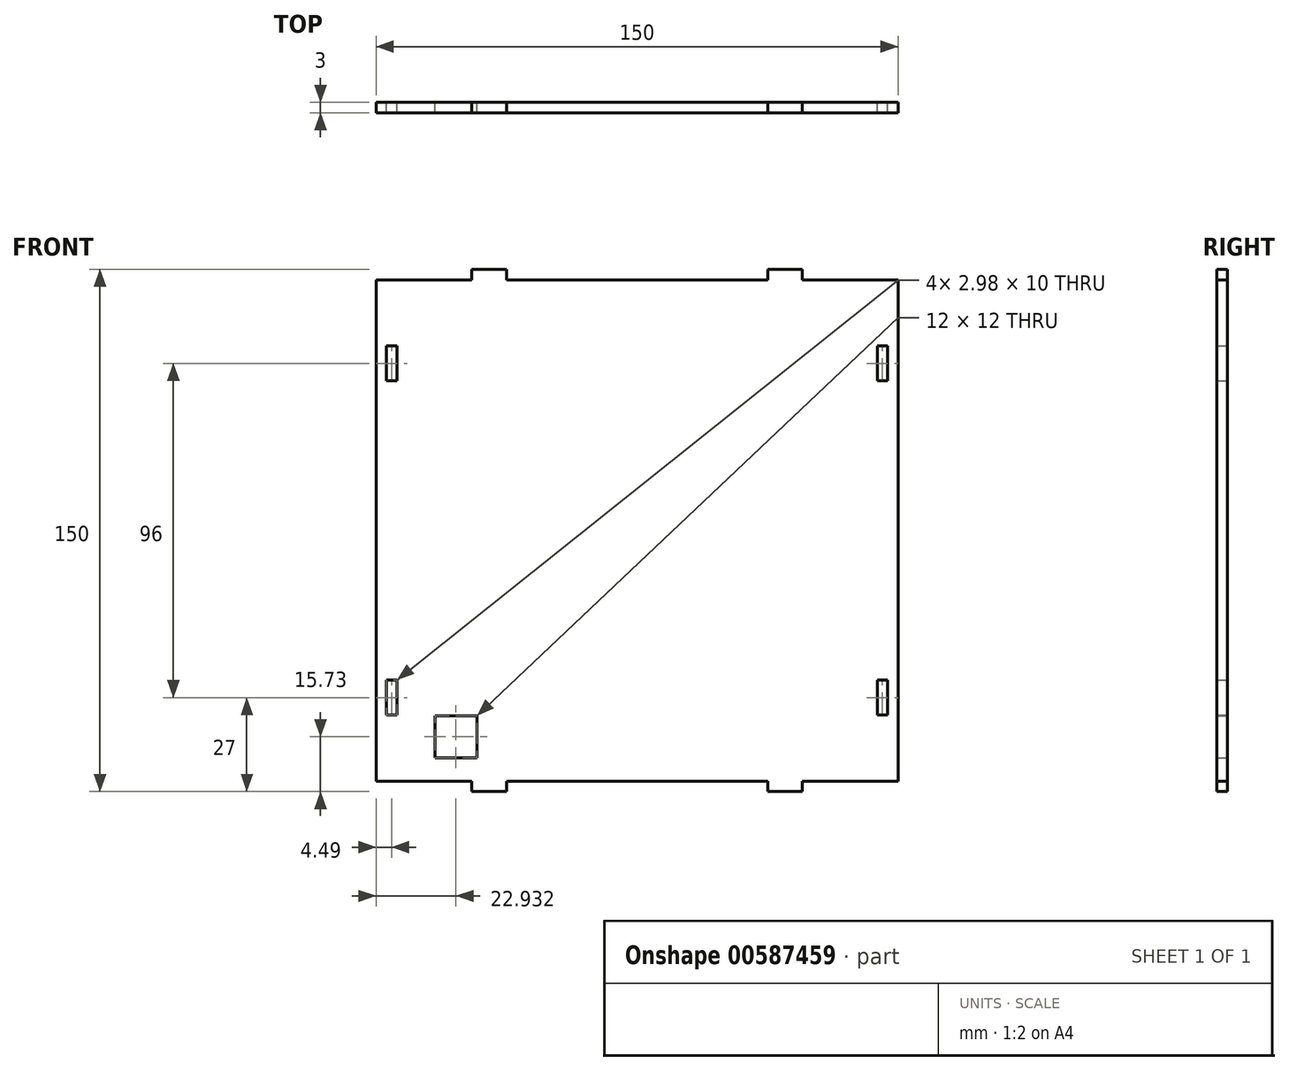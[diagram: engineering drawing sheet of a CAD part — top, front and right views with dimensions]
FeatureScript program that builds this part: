
annotation { "Feature Type Name" : "Feature", "Feature Type Description" : "" }
export const myFeature = defineFeature(function(context is Context, id is Id, definition is map)
    precondition{}
    {
        {
            var Q0;
            Q0=qCreatedBy(makeId("Front.planeOp"),FACE);
            var sketch = newSketch(context, id + "F0", { "sketchPlane" : qUnion([Q0])});
            skLineSegment(sketch, "E0.left", {"start": v(-75, 72) * mm, "end": v(-75, -72) * mm});
            skLineSegment(sketch, "E0.right", {"start": v(75, 72) * mm, "end": v(75, -72) * mm});
            skLineSegment(sketch, "E1", {"start": v(-75, -72) * mm, "end": v(-47.5, -72) * mm});
            skLineSegment(sketch, "E2", {"start": v(-47.5, -72) * mm, "end": v(-47.5, -75) * mm});
            skLineSegment(sketch, "E3", {"start": v(-47.5, -75) * mm, "end": v(-37.5, -75) * mm});
            skLineSegment(sketch, "E4", {"start": v(-37.5, -75) * mm, "end": v(-37.5, -72) * mm});
            skLineSegment(sketch, "E5", {"start": v(-37.5, -72) * mm, "end": v(37.5, -72) * mm});
            skLineSegment(sketch, "E6", {"start": v(37.5, -72) * mm, "end": v(37.5, -75) * mm});
            skLineSegment(sketch, "E7", {"start": v(37.5, -75) * mm, "end": v(47.5, -75) * mm});
            skLineSegment(sketch, "E8", {"start": v(47.5, -75) * mm, "end": v(47.5, -72) * mm});
            skLineSegment(sketch, "E9", {"start": v(47.5, -72) * mm, "end": v(75, -72) * mm});
            skLineSegment(sketch, "E10", {"start": v(0, 72) * mm, "end": v(0, -70.83) * mm, "construction": true});
            skLineSegment(sketch, "E11.bottom", {"start": v(-72, 53) * mm, "end": v(-69.02, 53) * mm});
            skLineSegment(sketch, "E11.top", {"start": v(-72, 43) * mm, "end": v(-69.02, 43) * mm});
            skLineSegment(sketch, "E11.left", {"start": v(-72, 53) * mm, "end": v(-72, 43) * mm});
            skLineSegment(sketch, "E11.right", {"start": v(-69.02, 53) * mm, "end": v(-69.02, 43) * mm});
            skLineSegment(sketch, "E12", {"start": v(-70.51, 53) * mm, "end": v(-70.51, 43) * mm, "construction": true});
            skLineSegment(sketch, "E13", {"start": v(-72, 48) * mm, "end": v(-69.02, 48) * mm, "construction": true});
            skLineSegment(sketch, "E14", {"start": v(75, 0) * mm, "end": v(-75, 0) * mm, "construction": true});
            skLineSegment(sketch, "E15.MirrorCS", {"start": v(72, 43) * mm, "end": v(69.02, 43) * mm});
            skLineSegment(sketch, "E16.MirrorCS", {"start": v(69.02, 53) * mm, "end": v(69.02, 43) * mm});
            skLineSegment(sketch, "E17.MirrorCS", {"start": v(72, 53) * mm, "end": v(69.02, 53) * mm});
            skLineSegment(sketch, "E18.MirrorCS", {"start": v(72, 48) * mm, "end": v(69.02, 48) * mm, "construction": true});
            skLineSegment(sketch, "E19.MirrorCS", {"start": v(72, 53) * mm, "end": v(72, 43) * mm});
            skLineSegment(sketch, "E20.MirrorCS", {"start": v(70.51, 53) * mm, "end": v(70.51, 43) * mm, "construction": true});
            skLineSegment(sketch, "E21.MirrorCS", {"start": v(72, -43) * mm, "end": v(69.02, -43) * mm});
            skLineSegment(sketch, "E22.MirrorCS", {"start": v(72, -53) * mm, "end": v(69.02, -53) * mm});
            skLineSegment(sketch, "E23.MirrorCS", {"start": v(69.02, -53) * mm, "end": v(69.02, -43) * mm});
            skLineSegment(sketch, "E24.MirrorCS", {"start": v(70.51, -53) * mm, "end": v(70.51, -43) * mm, "construction": true});
            skLineSegment(sketch, "E25.MirrorCS", {"start": v(72, -48) * mm, "end": v(69.02, -48) * mm, "construction": true});
            skLineSegment(sketch, "E26.MirrorCS", {"start": v(72, -53) * mm, "end": v(72, -43) * mm});
            skLineSegment(sketch, "E27.MirrorCS", {"start": v(-72, -43) * mm, "end": v(-69.02, -43) * mm});
            skLineSegment(sketch, "E28.MirrorCS", {"start": v(-72, -53) * mm, "end": v(-69.02, -53) * mm});
            skLineSegment(sketch, "E29.MirrorCS", {"start": v(-69.02, -53) * mm, "end": v(-69.02, -43) * mm});
            skLineSegment(sketch, "E30.MirrorCS", {"start": v(-70.51, -53) * mm, "end": v(-70.51, -43) * mm, "construction": true});
            skLineSegment(sketch, "E31.MirrorCS", {"start": v(-72, -48) * mm, "end": v(-69.02, -48) * mm, "construction": true});
            skLineSegment(sketch, "E32.MirrorCS", {"start": v(-72, -53) * mm, "end": v(-72, -43) * mm});
            skLineSegment(sketch, "E33", {"start": v(-75, 72) * mm, "end": v(-47.5, 72) * mm});
            skLineSegment(sketch, "E34", {"start": v(-47.5, 72) * mm, "end": v(-47.5, 75) * mm});
            skLineSegment(sketch, "E35", {"start": v(-47.5, 75) * mm, "end": v(-37.5, 75) * mm});
            skLineSegment(sketch, "E36", {"start": v(-37.5, 75) * mm, "end": v(-37.5, 72) * mm});
            skLineSegment(sketch, "E37", {"start": v(-37.5, 72) * mm, "end": v(37.5, 72) * mm});
            skLineSegment(sketch, "E38", {"start": v(37.5, 72) * mm, "end": v(37.5, 75) * mm});
            skLineSegment(sketch, "E39", {"start": v(37.5, 75) * mm, "end": v(47.5, 75) * mm});
            skLineSegment(sketch, "E40", {"start": v(47.5, 75) * mm, "end": v(47.5, 72) * mm});
            skLineSegment(sketch, "E41", {"start": v(47.5, 72) * mm, "end": v(75, 72) * mm});
            skLineSegment(sketch, "E42.bottom", {"start": v(-58.07, -53.27) * mm, "end": v(-46.07, -53.27) * mm});
            skLineSegment(sketch, "E42.top", {"start": v(-58.07, -65.27) * mm, "end": v(-46.07, -65.27) * mm});
            skLineSegment(sketch, "E42.left", {"start": v(-58.07, -53.27) * mm, "end": v(-58.07, -65.27) * mm});
            skLineSegment(sketch, "E42.right", {"start": v(-46.07, -53.27) * mm, "end": v(-46.07, -65.27) * mm});
            skSolve(sketch);
        }
        {
            var Q0;
            Q0 = qSketchRegion(id + "F0", true);
            extrude(context, id + "F1", {"entities" : qUnion([Q0]), "depth" : 3 * mm, "offsetDistance" : 25 * mm});
        }
    });
